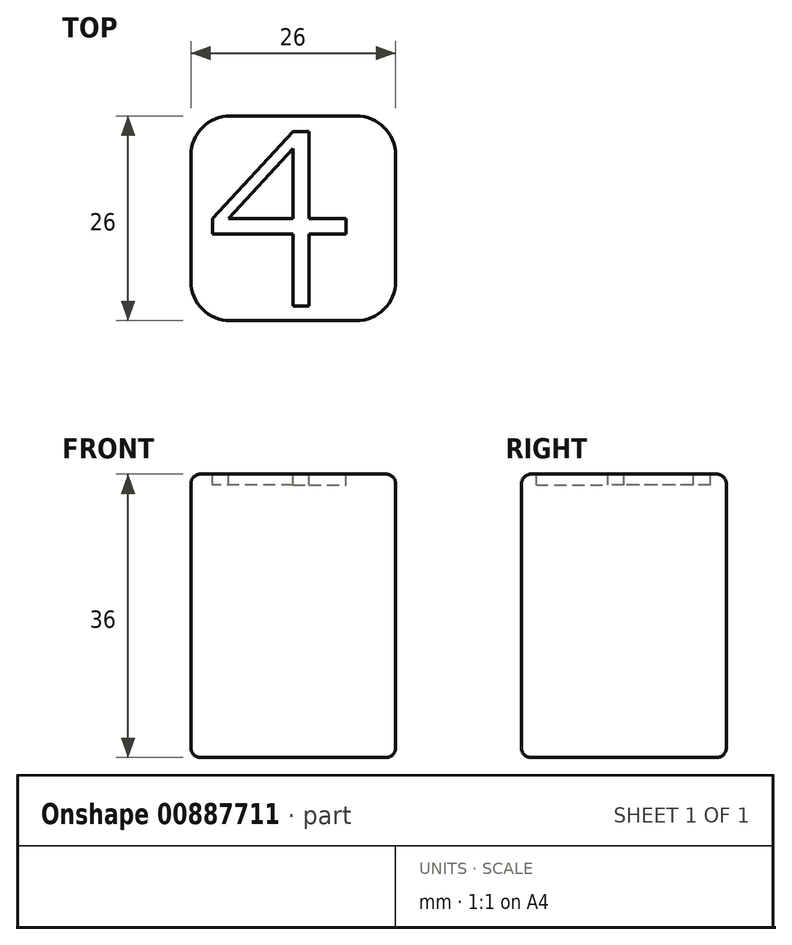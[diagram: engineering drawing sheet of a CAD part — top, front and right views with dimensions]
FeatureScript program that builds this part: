
annotation { "Feature Type Name" : "Feature", "Feature Type Description" : "" }
export const myFeature = defineFeature(function(context is Context, id is Id, definition is map)
    precondition{}
    {
        {
            var Q0;
            Q0=qCreatedBy(makeId("Top.planeOp"),FACE);
            var sketch = newSketch(context, id + "F0", { "sketchPlane" : qUnion([Q0])});
            skLineSegment(sketch, "E0", {"start": v(13, 0) * mm, "end": v(13, 13) * mm});
            skLineSegment(sketch, "E1.bottom", {"start": v(-13, -13) * mm, "end": v(13, -13) * mm});
            skLineSegment(sketch, "E1.top", {"start": v(-13, 13) * mm, "end": v(13, 13) * mm});
            skLineSegment(sketch, "E1.left", {"start": v(-13, -13) * mm, "end": v(-13, 13) * mm});
            skLineSegment(sketch, "E1.right", {"start": v(13, -13) * mm, "end": v(13, 13) * mm});
            skLineSegment(sketch, "E2", {"start": v(0, 11) * mm, "end": v(-10.25, 0) * mm});
            skLineSegment(sketch, "E3", {"start": v(-10.25, 0) * mm, "end": v(6.73, 0) * mm});
            skLineSegment(sketch, "E4", {"start": v(0, 11) * mm, "end": v(2, 11) * mm});
            skLineSegment(sketch, "E5", {"start": v(2, 11) * mm, "end": v(2, -11.12) * mm});
            skLineSegment(sketch, "E6", {"start": v(2, -11.12) * mm, "end": v(0, -11.12) * mm});
            skLineSegment(sketch, "E7", {"start": v(0, -11.12) * mm, "end": v(0, 11) * mm});
            skLineSegment(sketch, "E8", {"start": v(2, 11) * mm, "end": v(-8.25, 0) * mm});
            skLineSegment(sketch, "E9", {"start": v(6.73, 0) * mm, "end": v(6.73, -2) * mm});
            skLineSegment(sketch, "E10", {"start": v(-10.25, 0) * mm, "end": v(-10.25, -2) * mm});
            skLineSegment(sketch, "E11", {"start": v(-10.25, -2) * mm, "end": v(6.73, -2) * mm});
            skSolve(sketch);
        }
        {
            var Q0;
            {var subQ5=sQuery(id+"F0.wireOp",EDGE,"E1.bottom");Q0=makeQuery(id+"F0.imprint","IMPRINT",FACE,{"disambiguationData":[TD([[makeQuery(id+"F0.imprint","IMPRINT",EDGE,{"derivedFrom":subQ5}),1.0]])]});}
            var Q1;
            {var subQ0=sQuery(id+"F0.wireOp",EDGE,"E2");Q1=makeQuery(id+"F0.imprint","IMPRINT",FACE,{"disambiguationData":[TD([[makeQuery(id+"F0.imprint","IMPRINT",EDGE,{"derivedFrom":subQ0}),1.0]])]});}
            var Q2;
            {var subQ0=sQuery(id+"F0.wireOp",EDGE,"E10");Q2=makeQuery(id+"F0.imprint","IMPRINT",FACE,{"disambiguationData":[TD([[makeQuery(id+"F0.imprint","IMPRINT",EDGE,{"derivedFrom":subQ0}),1.0]])]});}
            var Q3;
            {var subQ0=sQuery(id+"F0.wireOp",EDGE,"E8");var subQ1=sQuery(id+"F0.wireOp",EDGE,"E3");var subQ2=makeQuery(id+"F0.imprint","INTERSECT",VERTEX,{"derivedFrom":[subQ1,subQ0]});Q3=makeQuery(id+"F0.imprint","IMPRINT",FACE,{"disambiguationData":[TD([[makeQuery(id+"F0.imprint","IMPRINT",EDGE,{"disambiguationData":[TD([[subQ2,-1.0]])],"derivedFrom":subQ1}),1.0]])]});}
            var Q4;
            {var subQ0=sQuery(id+"F0.wireOp",EDGE,"E7");var subQ1=sQuery(id+"F0.wireOp",EDGE,"E3");var subQ2=makeQuery(id+"F0.imprint","INTERSECT",VERTEX,{"derivedFrom":[subQ1,subQ0]});Q4=makeQuery(id+"F0.imprint","IMPRINT",FACE,{"disambiguationData":[TD([[makeQuery(id+"F0.imprint","IMPRINT",EDGE,{"disambiguationData":[TD([[subQ2,-1.0]])],"derivedFrom":subQ1}),1.0]])]});}
            var Q5;
            {var subQ0=sQuery(id+"F0.wireOp",EDGE,"E4");Q5=makeQuery(id+"F0.imprint","IMPRINT",FACE,{"disambiguationData":[TD([[makeQuery(id+"F0.imprint","IMPRINT",EDGE,{"derivedFrom":subQ0}),-1.0]])]});}
            var Q6;
            {var subQ0=sQuery(id+"F0.wireOp",EDGE,"E7");var subQ1=sQuery(id+"F0.wireOp",EDGE,"E3");var subQ2=makeQuery(id+"F0.imprint","INTERSECT",VERTEX,{"derivedFrom":[subQ1,subQ0]});Q6=makeQuery(id+"F0.imprint","IMPRINT",FACE,{"disambiguationData":[TD([[makeQuery(id+"F0.imprint","IMPRINT",EDGE,{"disambiguationData":[TD([[subQ2,-1.0]])],"derivedFrom":subQ1}),-1.0]])]});}
            var Q7;
            {var subQ0=sQuery(id+"F0.wireOp",EDGE,"E6");Q7=makeQuery(id+"F0.imprint","IMPRINT",FACE,{"disambiguationData":[TD([[makeQuery(id+"F0.imprint","IMPRINT",EDGE,{"derivedFrom":subQ0}),-1.0]])]});}
            var Q8;
            {var subQ0=sQuery(id+"F0.wireOp",EDGE,"E9");Q8=makeQuery(id+"F0.imprint","IMPRINT",FACE,{"disambiguationData":[TD([[makeQuery(id+"F0.imprint","IMPRINT",EDGE,{"derivedFrom":subQ0}),-1.0]])]});}
            extrude(context, id + "F1", {"entities" : qUnion([Q0, Q1, Q2, Q3, Q4, Q5, Q6, Q7, Q8]), "oppositeDirection" : true, "depth" : 36 * mm, "offsetDistance" : 25 * mm});
        }
        {
            var Q0;
            {var subQ0=sQuery(id+"F0.wireOp",EDGE,"E2");Q0=makeQuery(id+"F0.imprint","IMPRINT",FACE,{"disambiguationData":[TD([[makeQuery(id+"F0.imprint","IMPRINT",EDGE,{"derivedFrom":subQ0}),1.0]])]});}
            var Q1;
            {var subQ0=sQuery(id+"F0.wireOp",EDGE,"E4");Q1=makeQuery(id+"F0.imprint","IMPRINT",FACE,{"disambiguationData":[TD([[makeQuery(id+"F0.imprint","IMPRINT",EDGE,{"derivedFrom":subQ0}),-1.0]])]});}
            var Q2;
            {var subQ0=sQuery(id+"F0.wireOp",EDGE,"E7");var subQ1=sQuery(id+"F0.wireOp",EDGE,"E3");var subQ2=makeQuery(id+"F0.imprint","INTERSECT",VERTEX,{"derivedFrom":[subQ1,subQ0]});Q2=makeQuery(id+"F0.imprint","IMPRINT",FACE,{"disambiguationData":[TD([[makeQuery(id+"F0.imprint","IMPRINT",EDGE,{"disambiguationData":[TD([[subQ2,-1.0]])],"derivedFrom":subQ1}),1.0]])]});}
            var Q3;
            {var subQ0=sQuery(id+"F0.wireOp",EDGE,"E9");Q3=makeQuery(id+"F0.imprint","IMPRINT",FACE,{"disambiguationData":[TD([[makeQuery(id+"F0.imprint","IMPRINT",EDGE,{"derivedFrom":subQ0}),-1.0]])]});}
            var Q4;
            {var subQ0=sQuery(id+"F0.wireOp",EDGE,"E6");Q4=makeQuery(id+"F0.imprint","IMPRINT",FACE,{"disambiguationData":[TD([[makeQuery(id+"F0.imprint","IMPRINT",EDGE,{"derivedFrom":subQ0}),-1.0]])]});}
            var Q5;
            {var subQ0=sQuery(id+"F0.wireOp",EDGE,"E7");var subQ1=sQuery(id+"F0.wireOp",EDGE,"E3");var subQ2=makeQuery(id+"F0.imprint","INTERSECT",VERTEX,{"derivedFrom":[subQ1,subQ0]});Q5=makeQuery(id+"F0.imprint","IMPRINT",FACE,{"disambiguationData":[TD([[makeQuery(id+"F0.imprint","IMPRINT",EDGE,{"disambiguationData":[TD([[subQ2,-1.0]])],"derivedFrom":subQ1}),-1.0]])]});}
            var Q6;
            {var subQ0=sQuery(id+"F0.wireOp",EDGE,"E10");Q6=makeQuery(id+"F0.imprint","IMPRINT",FACE,{"disambiguationData":[TD([[makeQuery(id+"F0.imprint","IMPRINT",EDGE,{"derivedFrom":subQ0}),1.0]])]});}
            extrude(context, id + "F2", {"entities" : qUnion([Q0, Q1, Q2, Q3, Q4, Q5, Q6]), "operationType" : NewBodyOperationType.REMOVE, "oppositeDirection" : true, "depth" : 1.4 * mm, "offsetDistance" : 25 * mm});
        }
        {
            var Q0;
            Q0=makeQuery(id+"F1.opExtrude","SWEPT_EDGE",EDGE,{"disambiguationData":[OSD([sQuery(id+"F0.wireOp",EDGE,"E1.top"),sQuery(id+"F0.wireOp",EDGE,"E1.right")])]});
            var Q1;
            Q1=makeQuery(id+"F1.opExtrude","SWEPT_EDGE",EDGE,{"disambiguationData":[OSD([sQuery(id+"F0.wireOp",EDGE,"E1.bottom"),sQuery(id+"F0.wireOp",EDGE,"E1.right")])]});
            var Q2;
            Q2=makeQuery(id+"F1.opExtrude","SWEPT_EDGE",EDGE,{"disambiguationData":[OSD([sQuery(id+"F0.wireOp",EDGE,"E1.bottom"),sQuery(id+"F0.wireOp",EDGE,"E1.left")])]});
            var Q3;
            Q3=makeQuery(id+"F1.opExtrude","SWEPT_EDGE",EDGE,{"disambiguationData":[OSD([sQuery(id+"F0.wireOp",EDGE,"E1.top"),sQuery(id+"F0.wireOp",EDGE,"E1.left")])]});
            fillet(context, id + "F3", {"entities" : qUnion([Q0, Q1, Q2, Q3]), "radius" : 5 * mm, "tangentPropagation" : true, "allowEdgeOverflow" : false});
        }
        {
            var Q0;
            Q0=makeQuery(id+"F1.opExtrude","CAP_EDGE",EDGE,{"disambiguationData":[OSD([sQuery(id+"F0.wireOp",EDGE,"E1.left")])],"isStart":true});
            var Q1;
            {var subQ8=sQuery(id+"F0.wireOp",EDGE,"E1.bottom");var subQ12=sQuery(id+"F0.wireOp",EDGE,"E1.right");var subQ13=sQuery(id+"F0.wireOp",EDGE,"E1.top");var subQ14=sQuery(id+"F0.wireOp",EDGE,"E1.left");Q1=makeQuery(id+"F3.opFillet","BLEND_EDGE",EDGE,{"blendedFrom":[makeQuery(id+"F1.opExtrude","SWEPT_EDGE",EDGE,{"disambiguationData":[OSD([subQ13,subQ14])]}),makeQuery(id+"F2.boolean.opBoolean","SPLIT",FACE,{"disambiguationData":[TD([makeQuery(id+"F1.opExtrude","SWEPT_FACE",FACE,{"disambiguationData":[OSD([subQ8])]})])],"derivedFrom":makeQuery(id+"F1.opExtrude","CAP_FACE",FACE,{"disambiguationData":[OSD([subQ8,subQ13,subQ14,subQ12])],"isStart":true})})],"blendedInto":[makeQuery(id+"F2.boolean.opBoolean","SPLIT",FACE,{"disambiguationData":[TD([makeQuery(id+"F1.opExtrude","SWEPT_FACE",FACE,{"disambiguationData":[OSD([subQ8])]})])],"derivedFrom":makeQuery(id+"F1.opExtrude","CAP_FACE",FACE,{"disambiguationData":[OSD([subQ8,subQ13,subQ14,subQ12])],"isStart":true})})]});}
            var Q2;
            Q2=makeQuery(id+"F1.opExtrude","CAP_EDGE",EDGE,{"disambiguationData":[OSD([sQuery(id+"F0.wireOp",EDGE,"E1.top")])],"isStart":true});
            var Q3;
            {var subQ8=sQuery(id+"F0.wireOp",EDGE,"E1.bottom");var subQ12=sQuery(id+"F0.wireOp",EDGE,"E1.right");var subQ13=sQuery(id+"F0.wireOp",EDGE,"E1.top");var subQ14=sQuery(id+"F0.wireOp",EDGE,"E1.left");Q3=makeQuery(id+"F3.opFillet","BLEND_EDGE",EDGE,{"blendedFrom":[makeQuery(id+"F1.opExtrude","SWEPT_EDGE",EDGE,{"disambiguationData":[OSD([subQ8,subQ14])]}),makeQuery(id+"F2.boolean.opBoolean","SPLIT",FACE,{"disambiguationData":[TD([makeQuery(id+"F1.opExtrude","SWEPT_FACE",FACE,{"disambiguationData":[OSD([subQ8])]})])],"derivedFrom":makeQuery(id+"F1.opExtrude","CAP_FACE",FACE,{"disambiguationData":[OSD([subQ8,subQ13,subQ14,subQ12])],"isStart":true})})],"blendedInto":[makeQuery(id+"F2.boolean.opBoolean","SPLIT",FACE,{"disambiguationData":[TD([makeQuery(id+"F1.opExtrude","SWEPT_FACE",FACE,{"disambiguationData":[OSD([subQ8])]})])],"derivedFrom":makeQuery(id+"F1.opExtrude","CAP_FACE",FACE,{"disambiguationData":[OSD([subQ8,subQ13,subQ14,subQ12])],"isStart":true})})]});}
            var Q4;
            Q4=makeQuery(id+"F1.opExtrude","CAP_EDGE",EDGE,{"disambiguationData":[OSD([sQuery(id+"F0.wireOp",EDGE,"E1.bottom")])],"isStart":true});
            var Q5;
            {var subQ8=sQuery(id+"F0.wireOp",EDGE,"E1.bottom");var subQ12=sQuery(id+"F0.wireOp",EDGE,"E1.right");var subQ13=sQuery(id+"F0.wireOp",EDGE,"E1.top");var subQ14=sQuery(id+"F0.wireOp",EDGE,"E1.left");Q5=makeQuery(id+"F3.opFillet","BLEND_EDGE",EDGE,{"blendedFrom":[makeQuery(id+"F1.opExtrude","SWEPT_EDGE",EDGE,{"disambiguationData":[OSD([subQ8,subQ12])]}),makeQuery(id+"F2.boolean.opBoolean","SPLIT",FACE,{"disambiguationData":[TD([makeQuery(id+"F1.opExtrude","SWEPT_FACE",FACE,{"disambiguationData":[OSD([subQ8])]})])],"derivedFrom":makeQuery(id+"F1.opExtrude","CAP_FACE",FACE,{"disambiguationData":[OSD([subQ8,subQ13,subQ14,subQ12])],"isStart":true})})],"blendedInto":[makeQuery(id+"F2.boolean.opBoolean","SPLIT",FACE,{"disambiguationData":[TD([makeQuery(id+"F1.opExtrude","SWEPT_FACE",FACE,{"disambiguationData":[OSD([subQ8])]})])],"derivedFrom":makeQuery(id+"F1.opExtrude","CAP_FACE",FACE,{"disambiguationData":[OSD([subQ8,subQ13,subQ14,subQ12])],"isStart":true})})]});}
            var Q6;
            Q6=makeQuery(id+"F1.opExtrude","CAP_EDGE",EDGE,{"disambiguationData":[OSD([sQuery(id+"F0.wireOp",EDGE,"E1.right")])],"isStart":true});
            var Q7;
            {var subQ8=sQuery(id+"F0.wireOp",EDGE,"E1.bottom");var subQ12=sQuery(id+"F0.wireOp",EDGE,"E1.right");var subQ13=sQuery(id+"F0.wireOp",EDGE,"E1.top");var subQ14=sQuery(id+"F0.wireOp",EDGE,"E1.left");Q7=makeQuery(id+"F3.opFillet","BLEND_EDGE",EDGE,{"blendedFrom":[makeQuery(id+"F1.opExtrude","SWEPT_EDGE",EDGE,{"disambiguationData":[OSD([subQ13,subQ12])]}),makeQuery(id+"F2.boolean.opBoolean","SPLIT",FACE,{"disambiguationData":[TD([makeQuery(id+"F1.opExtrude","SWEPT_FACE",FACE,{"disambiguationData":[OSD([subQ8])]})])],"derivedFrom":makeQuery(id+"F1.opExtrude","CAP_FACE",FACE,{"disambiguationData":[OSD([subQ8,subQ13,subQ14,subQ12])],"isStart":true})})],"blendedInto":[makeQuery(id+"F2.boolean.opBoolean","SPLIT",FACE,{"disambiguationData":[TD([makeQuery(id+"F1.opExtrude","SWEPT_FACE",FACE,{"disambiguationData":[OSD([subQ8])]})])],"derivedFrom":makeQuery(id+"F1.opExtrude","CAP_FACE",FACE,{"disambiguationData":[OSD([subQ8,subQ13,subQ14,subQ12])],"isStart":true})})]});}
            var Q8;
            Q8=makeQuery(id+"F1.opExtrude","CAP_FACE",FACE,{"disambiguationData":[OSD([sQuery(id+"F0.wireOp",EDGE,"E1.bottom"),sQuery(id+"F0.wireOp",EDGE,"E1.top"),sQuery(id+"F0.wireOp",EDGE,"E1.left"),sQuery(id+"F0.wireOp",EDGE,"E1.right")])],"isStart":false});
            fillet(context, id + "F4", {"entities" : qUnion([Q0, Q1, Q2, Q3, Q4, Q5, Q6, Q7, Q8]), "radius" : 1.2 * mm, "tangentPropagation" : true, "allowEdgeOverflow" : false});
        }
    });
